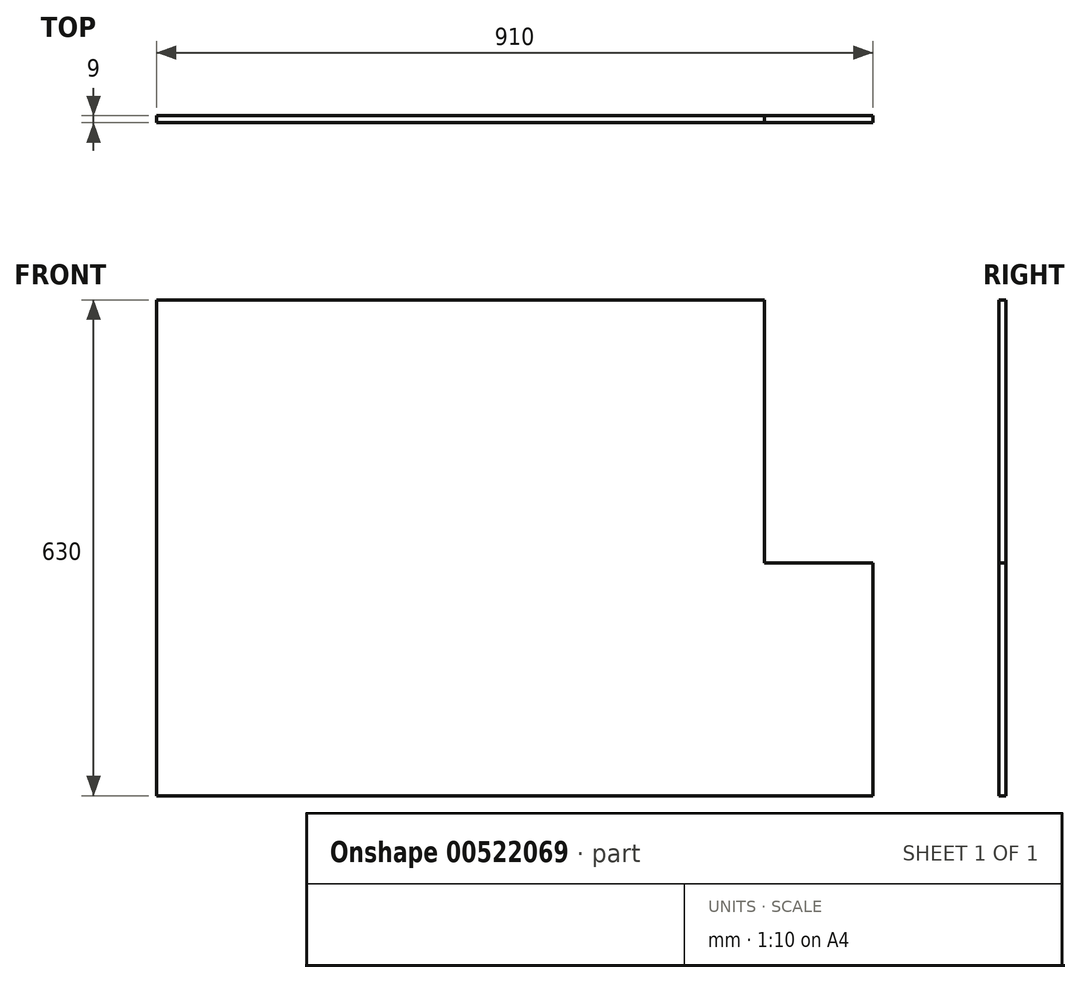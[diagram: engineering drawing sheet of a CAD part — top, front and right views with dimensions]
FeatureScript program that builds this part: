
annotation { "Feature Type Name" : "Feature", "Feature Type Description" : "" }
export const myFeature = defineFeature(function(context is Context, id is Id, definition is map)
    precondition{}
    {
        {
            var Q0;
            Q0=qCreatedBy(makeId("Front.planeOp"),FACE);
            var sketch = newSketch(context, id + "F0", { "sketchPlane" : qUnion([Q0])});
            skLineSegment(sketch, "E0.bottom", {"start": v(0, 0) * mm, "end": v(-910, 0) * mm});
            skLineSegment(sketch, "E0.top", {"start": v(-138, 630) * mm, "end": v(-910, 630) * mm});
            skLineSegment(sketch, "E0.left", {"start": v(0, 0) * mm, "end": v(0, 296) * mm});
            skLineSegment(sketch, "E0.right", {"start": v(-910, 0) * mm, "end": v(-910, 630) * mm});
            skLineSegment(sketch, "E1", {"start": v(-138, 630) * mm, "end": v(-138, 296) * mm});
            skLineSegment(sketch, "E2", {"start": v(-138, 296) * mm, "end": v(0, 296) * mm});
            skSolve(sketch);
        }
        {
            var Q0;
            Q0=makeQuery(id+"F0.imprint","IMPRINT",FACE,{"disambiguationData":[TD([[makeQuery(id+"F0.imprint","IMPRINT",EDGE,{"derivedFrom":sQuery(id+"F0.wireOp",EDGE,"E0.bottom")}),-1.0]])]});
            extrude(context, id + "F1", {"entities" : qUnion([Q0]), "depth" : 9 * mm, "offsetDistance" : 25 * mm});
        }
    });
